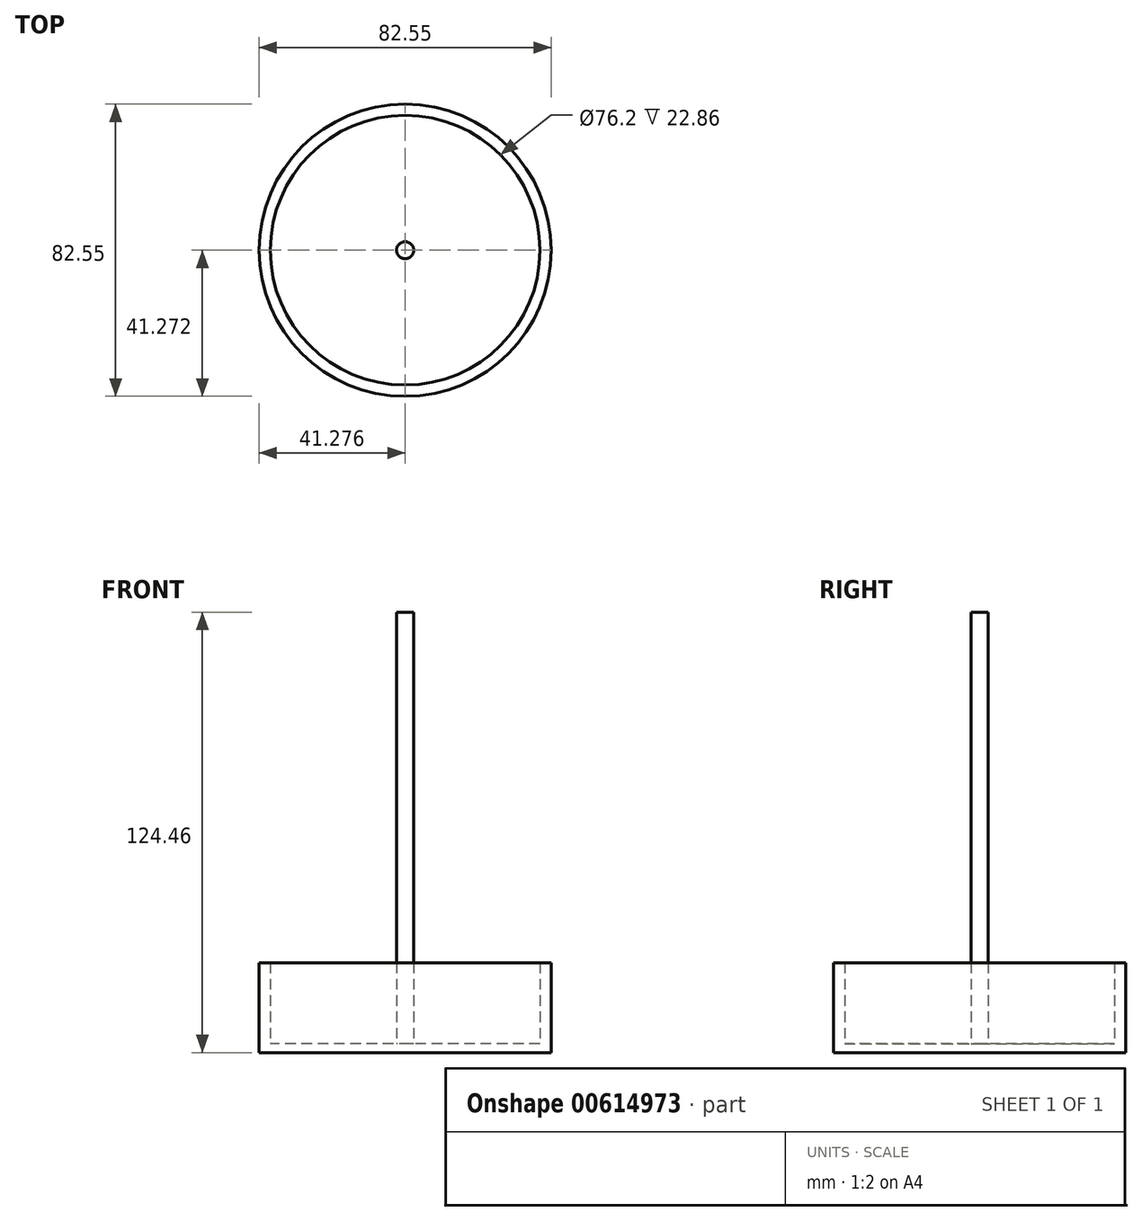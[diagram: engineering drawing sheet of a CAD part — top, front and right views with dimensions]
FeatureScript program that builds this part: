
annotation { "Feature Type Name" : "Feature", "Feature Type Description" : "" }
export const myFeature = defineFeature(function(context is Context, id is Id, definition is map)
    precondition{}
    {
        {
            var Q0;
            Q0=qCreatedBy(makeId("Top.planeOp"),FACE);
            var sketch = newSketch(context, id + "F0", { "sketchPlane" : qUnion([Q0])});
            skCircle(sketch, "E0", {"center": v(-94.07, 5.04) * mm, "radius": 41.28 * mm});
            skCircle(sketch, "E1", {"center": v(-94.07, 5.04) * mm, "radius": 38.1 * mm});
            skCircle(sketch, "E2", {"center": v(-94.07, 5.04) * mm, "radius": 2.41 * mm});
            skSolve(sketch);
        }
        {
            var Q0;
            Q0=makeQuery(id+"F0.imprint","IMPRINT",FACE,{"disambiguationData":[TD([[makeQuery(id+"F0.imprint","IMPRINT",EDGE,{"derivedFrom":sQuery(id+"F0.wireOp",EDGE,"E1")}),1.0]])]});
            extrude(context, id + "F1", {"entities" : qUnion([Q0]), "depth" : 2.54 * mm, "offsetDistance" : 25.4 * mm});
        }
        {
            var Q0;
            Q0=makeQuery(id+"F0.imprint","IMPRINT",FACE,{"disambiguationData":[TD([[makeQuery(id+"F0.imprint","IMPRINT",EDGE,{"derivedFrom":sQuery(id+"F0.wireOp",EDGE,"E0")}),1.0]])]});
            extrude(context, id + "F2", {"entities" : qUnion([Q0]), "operationType" : NewBodyOperationType.ADD, "depth" : 25.4 * mm, "offsetDistance" : 25.4 * mm});
        }
        {
            var Q0;
            Q0=makeQuery(id+"F0.imprint","IMPRINT",FACE,{"disambiguationData":[TD([[makeQuery(id+"F0.imprint","IMPRINT",EDGE,{"derivedFrom":sQuery(id+"F0.wireOp",EDGE,"E1")}),1.0]])]});
            var sketch = newSketch(context, id + "F3", { "sketchPlane" : qUnion([Q0])});
            skCircle(sketch, "E3.0", {"center": v(-94.07, 5.04) * mm, "radius": 2.41 * mm});
            skSolve(sketch);
        }
        {
            var Q0;
            Q0 = qSketchRegion(id + "F3", true);
            extrude(context, id + "F4", {"entities" : qUnion([Q0]), "operationType" : NewBodyOperationType.ADD, "depth" : 124.46 * mm, "offsetDistance" : 25.4 * mm});
        }
    });
